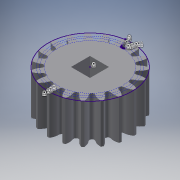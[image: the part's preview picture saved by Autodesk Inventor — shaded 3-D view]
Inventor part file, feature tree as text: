
AUTODESK INVENTOR PART (.ipt)
format: ipt  version: 2017 (Build 210142000, 142)  size: 267,264 bytes
history: native  units: mm
features: extrude x3, sketch x2, pattern_circular x1
ambient origin geometry x8: Origin, YZ Plane, XZ Plane, XY Plane, X Axis, Y Axis, Z Axis, Center Point
bodies: Solid1 (feature_tree)
feature tree (6):
  sketch  "Sketch1"  dims[d0=20.0mm d1=0.0mm]
  extrude  "Extrusion1"  TaperAngle=0.0deg  [1 undecoded]
  extrude  "Extrusion2"  Depth=9.525mm TaperAngle=360.0deg
  pattern_circular  "Circular Pattern1"  [2 undecoded]
  extrude  "Extrusion3"  Depth=9.525mm TaperAngle=0.0deg
  sketch  "Sketch2"  dims[d2=10.0mm d3=0.0mm d4=190.0mm d5=360.0deg d7=9.525mm d8=10.0mm d9=0.0mm]
note: 3 required parameter values undecoded (feature->parameter linkage not recoverable at this tier; creation-order binding heuristic only, values carry confidence <= 0.55)
